# Revit family: AFX-Montclair-Flush_Mount
name_source: partatom
category: Lighting Fixtures
units: mm (PartAtom-declared; Revit-internal decimal feet)

## family parameters
Cut with Voids When Loaded = No
Host = Face
Light Source = Yes
Part Type = Normal
Room Calculation Point = No
Round Connector Dimension = Use Diameter
Shared = No

## types (5) — shared parameters
Apparent Load = 0 VA
Assembly Code = D5020200
Color Filter = 16777215
Colour Rendering Index = 80
Default Elevation = 48"
Diffuser Finish = AFX - White Acrylic
Dimming Lamp Color Temperature Shift = <None>
Emit Shape Visible in Rendering = No
Housing Finish = AFX - Fabric
Keynote = 12500
Manufacturer = AFX Inc
Photometric Web File = MCF193200LxxD1SN-BK_IES.ies
Power Factor = 1
Product Documentation Link = https://www.afxinc.com
Revit File Built By = https://servex-us.com
Supports Finish = AFX - Black Steel
Sustainability = https://lamprecycle.org
Tilt Angle = 90.00°
Type Comments = Montclair
URL = https://www.afxinc.com
Voltage = 120 V
Wattage Comments = 9

## per-type parameters (varying)
| type | Depth | Description | Diameter | Emit from Circle Diameter |
| MCF1214MBBK | 3 3/4" | Flush Mount - 12 1/4”Dia x 3 3/4”D | 12 1/4" | 12" |
| MCF1524MB-BK | 4 3/4" | Flush Mount - 15”Dia x 4 3/4”D | 15" | 15" |
| MCF1932MB-BK | 5 1/2" | Flush Mount - 19 1/4"Dia x 5 1/2"D | 19 1/4" | 19" |
| MCF2432MB-BK | 7 1/2" | Flush Mount - 24"Dia x 7 1/2"D | 24" | 24" |
| MCF3044MB-BK | 9 1/2" | Flush Mount -  30"Dia x 9 1/2"D | 30" | 30" |

note: column(s) folded — value = type name in every type: Model

## geometry (parser evidence)
native form markers: Sweep x2
no freeform markers — native parametric forms only
